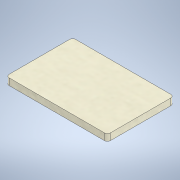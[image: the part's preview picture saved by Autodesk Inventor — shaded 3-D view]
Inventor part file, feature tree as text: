
AUTODESK INVENTOR PART (.ipt)
format: ipt  version: 2021 (Build 250183000, 183)  size: 111,616 bytes
history: native  units: mm
features: extrude x1, sketch x1
ambient origin geometry x8: Origin, YZ Plane, XZ Plane, XY Plane, X Axis, Y Axis, Z Axis, Center Point
bodies: Solid1 (feature_tree)
feature tree (2):
  extrude  "Extrusion1"  Depth=42.0mm
  sketch  "Sketch1"  dims[d0=64.0mm d1=42.0mm d2=2.0mm d3=4.25mm d4=0.0mm]
